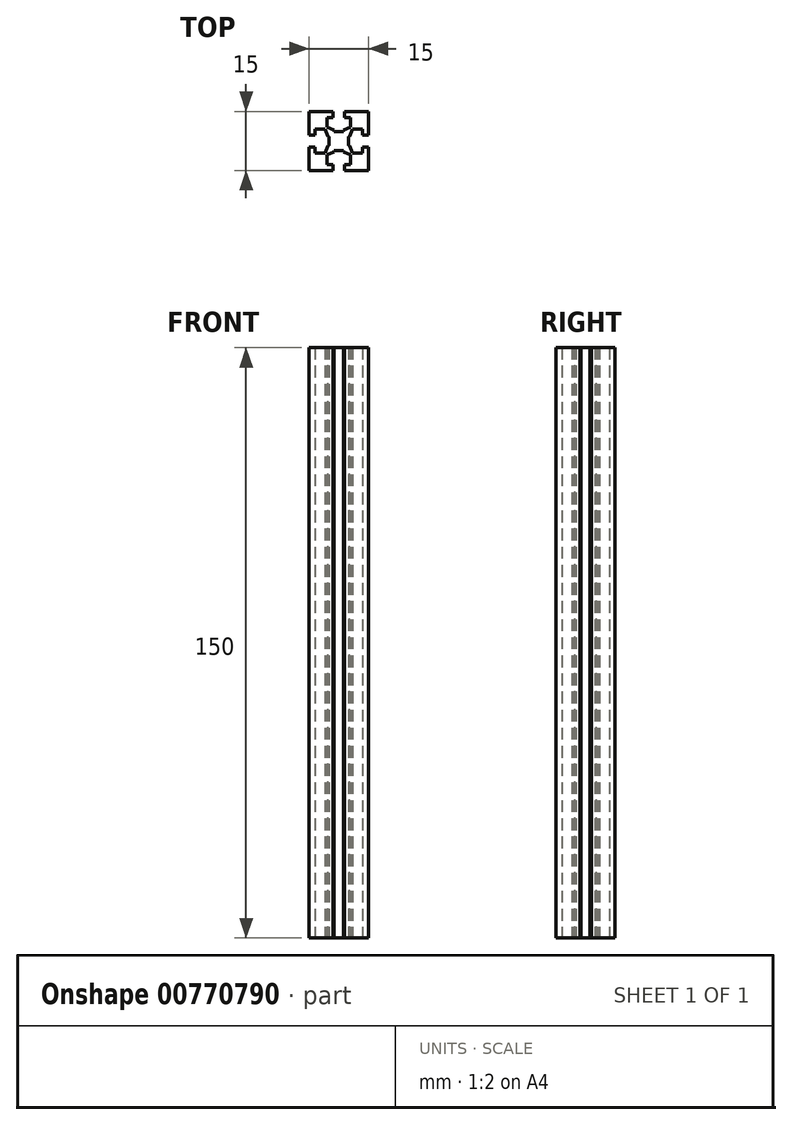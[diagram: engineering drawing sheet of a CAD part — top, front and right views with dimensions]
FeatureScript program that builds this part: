
annotation { "Feature Type Name" : "Feature", "Feature Type Description" : "" }
export const myFeature = defineFeature(function(context is Context, id is Id, definition is map)
    precondition{}
    {
        {
            var Q0;
            Q0=qCreatedBy(makeId("Top.planeOp"),FACE);
            var sketch = newSketch(context, id + "F0", { "sketchPlane" : qUnion([Q0])});
            skLineSegment(sketch, "E0.bottom", {"start": v(7.5, 7.5) * mm, "end": v(1.5, 7.5) * mm});
            skLineSegment(sketch, "E0.left", {"start": v(7.5, 7.5) * mm, "end": v(7.5, 1.5) * mm});
            skLineSegment(sketch, "E0.right", {"start": v(-7.5, 7.5) * mm, "end": v(-7.5, 1.5) * mm});
            skPoint(sketch, "E0.middle", {"position": v(0, 0) * mm});
            skLineSegment(sketch, "E1", {"start": v(7.5, -7.5) * mm, "end": v(1.5, -7.5) * mm});
            skLineSegment(sketch, "E2", {"start": v(1.5, -7.5) * mm, "end": v(1.5, -6) * mm});
            skLineSegment(sketch, "E3", {"start": v(1.5, -6) * mm, "end": v(3, -6) * mm});
            skLineSegment(sketch, "E4", {"start": v(3, -6) * mm, "end": v(3, -3.5) * mm});
            skLineSegment(sketch, "E5", {"start": v(-3, -3.5) * mm, "end": v(-3, -6) * mm});
            skLineSegment(sketch, "E6", {"start": v(-3, -6) * mm, "end": v(-1.5, -6) * mm});
            skLineSegment(sketch, "E7", {"start": v(-1.5, -6) * mm, "end": v(-1.5, -7.5) * mm});
            skLineSegment(sketch, "E8", {"start": v(-1.5, -7.5) * mm, "end": v(-7.5, -7.5) * mm});
            skLineSegment(sketch, "E9.top", {"start": v(1.15, -2.43) * mm, "end": v(-1.15, -2.43) * mm});
            skLineSegment(sketch, "E9.left", {"start": v(1.15, -2.76) * mm, "end": v(1.15, -2.43) * mm});
            skLineSegment(sketch, "E9.right", {"start": v(-1.15, -2.76) * mm, "end": v(-1.15, -2.43) * mm});
            skPoint(sketch, "E9.middle", {"position": v(0, -2.6) * mm});
            skLineSegment(sketch, "E10", {"start": v(-3, -3.5) * mm, "end": v(-1.15, -2.76) * mm});
            skLineSegment(sketch, "E11", {"start": v(3, -3.5) * mm, "end": v(1.15, -2.76) * mm});
            skLineSegment(sketch, "E12.1.0", {"start": v(6, -1.5) * mm, "end": v(7.5, -1.5) * mm});
            skLineSegment(sketch, "E12.1.1", {"start": v(6, -3) * mm, "end": v(6, -1.5) * mm});
            skLineSegment(sketch, "E12.1.2", {"start": v(3.5, -3) * mm, "end": v(6, -3) * mm});
            skLineSegment(sketch, "E12.1.3", {"start": v(3.5, -3) * mm, "end": v(2.76, -1.15) * mm});
            skLineSegment(sketch, "E12.1.4", {"start": v(2.43, 1.15) * mm, "end": v(2.43, -1.15) * mm});
            skLineSegment(sketch, "E12.1.5", {"start": v(2.76, 1.15) * mm, "end": v(2.43, 1.15) * mm});
            skLineSegment(sketch, "E12.1.6", {"start": v(2.76, -1.15) * mm, "end": v(2.43, -1.15) * mm});
            skLineSegment(sketch, "E12.1.7", {"start": v(3.5, 3) * mm, "end": v(2.76, 1.15) * mm});
            skLineSegment(sketch, "E12.1.8", {"start": v(6, 3) * mm, "end": v(3.5, 3) * mm});
            skLineSegment(sketch, "E12.1.9", {"start": v(6, 1.5) * mm, "end": v(6, 3) * mm});
            skLineSegment(sketch, "E12.1.10", {"start": v(7.5, 1.5) * mm, "end": v(6, 1.5) * mm});
            skLineSegment(sketch, "E12.2.0", {"start": v(1.5, 6) * mm, "end": v(1.5, 7.5) * mm});
            skLineSegment(sketch, "E12.2.1", {"start": v(3, 6) * mm, "end": v(1.5, 6) * mm});
            skLineSegment(sketch, "E12.2.2", {"start": v(3, 3.5) * mm, "end": v(3, 6) * mm});
            skLineSegment(sketch, "E12.2.3", {"start": v(3, 3.5) * mm, "end": v(1.15, 2.76) * mm});
            skLineSegment(sketch, "E12.2.4", {"start": v(-1.15, 2.43) * mm, "end": v(1.15, 2.43) * mm});
            skLineSegment(sketch, "E12.2.5", {"start": v(-1.15, 2.76) * mm, "end": v(-1.15, 2.43) * mm});
            skLineSegment(sketch, "E12.2.6", {"start": v(1.15, 2.76) * mm, "end": v(1.15, 2.43) * mm});
            skLineSegment(sketch, "E12.2.7", {"start": v(-3, 3.5) * mm, "end": v(-1.15, 2.76) * mm});
            skLineSegment(sketch, "E12.2.8", {"start": v(-3, 6) * mm, "end": v(-3, 3.5) * mm});
            skLineSegment(sketch, "E12.2.9", {"start": v(-1.5, 6) * mm, "end": v(-3, 6) * mm});
            skLineSegment(sketch, "E12.2.10", {"start": v(-1.5, 7.5) * mm, "end": v(-1.5, 6) * mm});
            skLineSegment(sketch, "E12.3.0", {"start": v(-6, 1.5) * mm, "end": v(-7.5, 1.5) * mm});
            skLineSegment(sketch, "E12.3.1", {"start": v(-6, 3) * mm, "end": v(-6, 1.5) * mm});
            skLineSegment(sketch, "E12.3.2", {"start": v(-3.5, 3) * mm, "end": v(-6, 3) * mm});
            skLineSegment(sketch, "E12.3.3", {"start": v(-3.5, 3) * mm, "end": v(-2.76, 1.15) * mm});
            skLineSegment(sketch, "E12.3.4", {"start": v(-2.43, -1.15) * mm, "end": v(-2.43, 1.15) * mm});
            skLineSegment(sketch, "E12.3.5", {"start": v(-2.76, -1.15) * mm, "end": v(-2.43, -1.15) * mm});
            skLineSegment(sketch, "E12.3.6", {"start": v(-2.76, 1.15) * mm, "end": v(-2.43, 1.15) * mm});
            skLineSegment(sketch, "E12.3.7", {"start": v(-3.5, -3) * mm, "end": v(-2.76, -1.15) * mm});
            skLineSegment(sketch, "E12.3.8", {"start": v(-6, -3) * mm, "end": v(-3.5, -3) * mm});
            skLineSegment(sketch, "E12.3.9", {"start": v(-6, -1.5) * mm, "end": v(-6, -3) * mm});
            skLineSegment(sketch, "E12.3.10", {"start": v(-7.5, -1.5) * mm, "end": v(-6, -1.5) * mm});
            skLineSegment(sketch, "E13.trimOffspring", {"start": v(-1.5, 7.5) * mm, "end": v(-7.5, 7.5) * mm});
            skLineSegment(sketch, "E14.trimOffspring", {"start": v(-7.5, -1.5) * mm, "end": v(-7.5, -7.5) * mm});
            skLineSegment(sketch, "E15.trimOffspring", {"start": v(7.5, -1.5) * mm, "end": v(7.5, -7.5) * mm});
            skSolve(sketch);
        }
        {
            var Q0;
            Q0=makeQuery(id+"F0.imprint","IMPRINT",FACE,{"disambiguationData":[TD([[makeQuery(id+"F0.imprint","IMPRINT",EDGE,{"derivedFrom":sQuery(id+"F0.wireOp",EDGE,"E0.bottom")}),1.0]])]});
            extrude(context, id + "F1", {"entities" : qUnion([Q0]), "endBound" : BoundingType.SYMMETRIC, "depth" : 150 * mm, "offsetDistance" : 25 * mm});
        }
    });
